# Revit family: RV4100 58 Kloss estanca
name_source: partatom
category: Luminarias
revit_build: Autodesk Revit 2015 (Build: 20140606_1530(x64)
units: mm (PartAtom-declared; Revit-internal decimal feet)

## types (3) — shared parameters
Anchura rectángulo de emisión = 120 mm  [stored 0.393701 ft]
Cambio de temperatura de color de luz atenuada = <Ninguno>
Fabricante = SECOM ILUMUNACIÓN
Filtro de color = 16777215
Forma visible en renderización = No
Longitud de rectángulo de emisión = 1060 mm  [stored 3.47769 ft]
Lámpara = LED Osram Duris E3
Modelo = Kloss estanca
Ángulo de inclinación = 90.00°

## per-type parameters (varying)
| type | Archivo de red fotométrica | Comentarios de vataje | Descripción |
| Kloss estanca 20W | 4100 58 20 84.IES | 20W | 4100 58 20 84 |
| Kloss estanca 40W | 4100 58 42 84.IES | 40W | 4100 58 40 84 |
| Kloss estanca 60W | 4100 58 60 84.IES | 60W | 4100 58 60 84 |

note: [stored X ft] marks values corroborated as IEEE doubles in the binary element streams (Revit-internal decimal feet)
